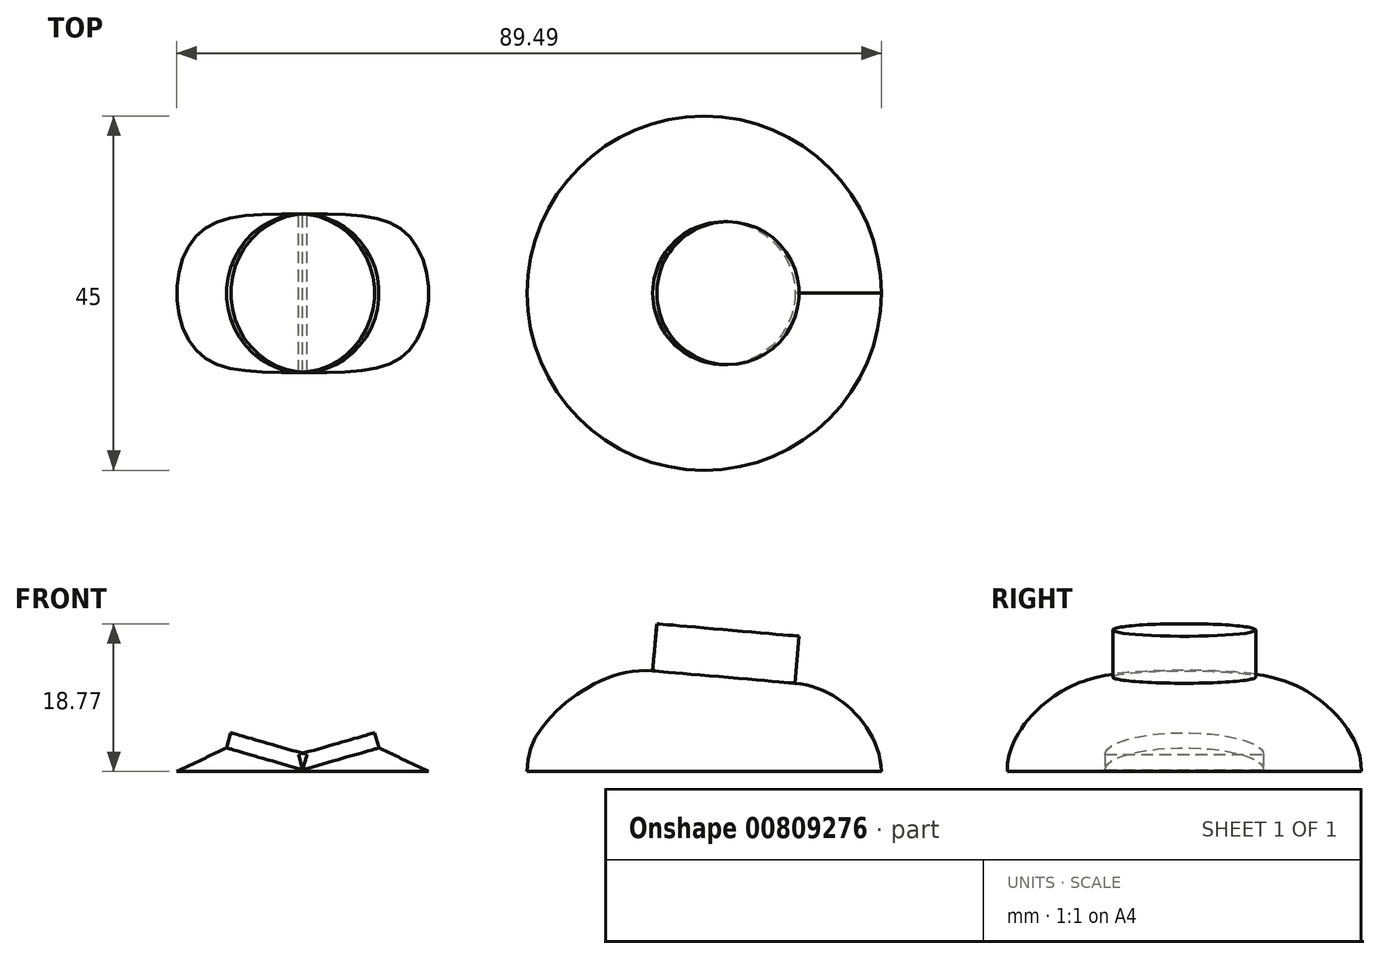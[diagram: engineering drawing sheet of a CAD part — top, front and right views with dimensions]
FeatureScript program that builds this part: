
annotation { "Feature Type Name" : "Feature", "Feature Type Description" : "" }
export const myFeature = defineFeature(function(context is Context, id is Id, definition is map)
    precondition{}
    {
        {
            var Q0;
            Q0=qCreatedBy(makeId("Top.planeOp"),FACE);
            cPlane(context, id + "F0", {"entities" : qUnion([Q0]), "cplaneType" : CPlaneType.OFFSET, "offset" : 12 * mm, "width" : 150 * mm, "height" : 150 * mm});
        }
        {
            var Q0;
            Q0=qCreatedBy(id+"F0.planeOp",FACE);
            var sketch = newSketch(context, id + "F1", { "sketchPlane" : qUnion([Q0])});
            skLineSegment(sketch, "E0", {"start": v(2.5, 4.56) * mm, "end": v(2.5, -4.56) * mm, "construction": true});
            skSolve(sketch);
        }
        {
            var Q0;
            Q0=sQuery(id+"F1.wireOp",EDGE,"E0");
            cPlane(context, id + "F2", {"entities" : qUnion([Q0]), "cplaneType" : CPlaneType.LINE_ANGLE, "offset" : 25 * mm, "angle" : 5 * degree, "oppositeDirection" : true, "width" : 150 * mm, "height" : 150 * mm});
        }
        {
            var Q0;
            Q0=qCreatedBy(id+"F2.planeOp",FACE);
            var sketch = newSketch(context, id + "F3", { "sketchPlane" : qUnion([Q0])});
            skPoint(sketch, "E1.0", {"position": v(1.44, 0) * mm});
            skCircle(sketch, "E2", {"center": v(1.44, 0) * mm, "radius": 9.07 * mm});
            skSolve(sketch);
        }
        {
            var Q0;
            Q0=qCreatedBy(makeId("Top.planeOp"),FACE);
            var sketch = newSketch(context, id + "F4", { "sketchPlane" : qUnion([Q0])});
            skCircle(sketch, "E3", {"center": v(0, 0) * mm, "radius": 22.5 * mm});
            skSolve(sketch);
        }
        {
            var Q0;
            Q0=qCreatedBy(makeId("Top.planeOp"),FACE);
            cPlane(context, id + "F5", {"entities" : qUnion([Q0]), "cplaneType" : CPlaneType.OFFSET, "offset" : 5 * mm, "width" : 150 * mm, "height" : 150 * mm});
        }
        {
            var Q0;
            Q0=qCreatedBy(id+"F5.planeOp",FACE);
            var sketch = newSketch(context, id + "F6", { "sketchPlane" : qUnion([Q0])});
            skCircle(sketch, "E4", {"center": v(0, 0) * mm, "radius": 21 * mm});
            skSolve(sketch);
        }
        {
            var Q0;
            Q0=makeQuery(id+"F4.imprint","IMPRINT",FACE,{"disambiguationData":[TD([[makeQuery(id+"F4.imprint","IMPRINT",EDGE,{"derivedFrom":sQuery(id+"F4.wireOp",EDGE,"E3")}),1.0]])]});
            var Q1;
            Q1=makeQuery(id+"F6.imprint","IMPRINT",FACE,{"disambiguationData":[TD([[makeQuery(id+"F6.imprint","IMPRINT",EDGE,{"derivedFrom":sQuery(id+"F6.wireOp",EDGE,"E4")}),1.0]])]});
            var Q2;
            Q2=makeQuery(id+"F3.imprint","IMPRINT",FACE,{"disambiguationData":[TD([[makeQuery(id+"F3.imprint","IMPRINT",EDGE,{"derivedFrom":sQuery(id+"F3.wireOp",EDGE,"E2")}),1.0]])]});
            loft(context, id + "F7", {"startCondition" : LoftEndDerivativeType.NORMAL_TO_PROFILE, "startMagnitude" : 1, "endCondition" : LoftEndDerivativeType.TANGENT_TO_PROFILE, "endMagnitude" : 1, "sheetProfilesArray" : [{ "sheetProfileEntities" : qUnion([Q0]) }, { "sheetProfileEntities" : qUnion([Q1]) }, { "sheetProfileEntities" : qUnion([Q2]) }]});
        }
        {
            var Q0;
            Q0=makeQuery(id+"F7.opLoft","CAP_FACE",FACE,{"disambiguationData":[OSD([makeQuery(id+"F3.imprint","IMPRINT",FACE,{"disambiguationData":[TD([[makeQuery(id+"F3.imprint","IMPRINT",EDGE,{"derivedFrom":sQuery(id+"F3.wireOp",EDGE,"E2")}),1.0]])]})])],"isStart":true});
            extrude(context, id + "F8", {"entities" : qUnion([Q0]), "operationType" : NewBodyOperationType.ADD, "depth" : 6 * mm, "offsetDistance" : 25 * mm});
        }
        {
            var Q0;
            Q0=qCreatedBy(makeId("Top.planeOp"),FACE);
            cPlane(context, id + "F9", {"entities" : qUnion([Q0]), "cplaneType" : CPlaneType.OFFSET, "offset" : 3 * mm, "width" : 150 * mm, "height" : 150 * mm});
        }
        {
            var Q0;
            Q0=qCreatedBy(id+"F9.planeOp",FACE);
            var sketch = newSketch(context, id + "F10", { "sketchPlane" : qUnion([Q0])});
            skLineSegment(sketch, "E5", {"start": v(-60.67, 23.33) * mm, "end": v(-60.67, -29.35) * mm, "construction": true});
            skSolve(sketch);
        }
        {
            var Q0;
            Q0=sQuery(id+"F10.wireOp",EDGE,"E5");
            cPlane(context, id + "F11", {"entities" : qUnion([Q0]), "cplaneType" : CPlaneType.LINE_ANGLE, "offset" : 25 * mm, "angle" : 16 * degree, "oppositeDirection" : true, "width" : 150 * mm, "height" : 150 * mm});
        }
        {
            var Q0;
            Q0=qCreatedBy(id+"F11.planeOp",FACE);
            var sketch = newSketch(context, id + "F12", { "sketchPlane" : qUnion([Q0])});
            skLineSegment(sketch, "E6.0", {"start": v(-59.15, -23.33) * mm, "end": v(-59.15, 29.35) * mm, "construction": true});
            skArc(sketch, "E7", {"start": v(-49.08, 10.07) * mm, "mid": v(-59.15, 0) * mm, "end": v(-49.08, -10.07) * mm});
            skLineSegment(sketch, "E8", {"start": v(-49.08, 10.07) * mm, "end": v(-49.08, -10.07) * mm});
            skSolve(sketch);
        }
        {
            var Q0;
            Q0=qCreatedBy(makeId("Top.planeOp"),FACE);
            var sketch = newSketch(context, id + "F13", { "sketchPlane" : qUnion([Q0])});
            skLineSegment(sketch, "E9.0", {"start": v(-50.99, -10.07) * mm, "end": v(-50.99, 10.07) * mm, "construction": true});
            skLineSegment(sketch, "E10", {"start": v(-66.99, -10.07) * mm, "end": v(-66.99, 10.07) * mm, "construction": true});
            skFitSpline(sketch, "E11", {"points": [v(-50.99, -10.07) * mm, v(-63.74, -8) * mm, v(-66.99, 0) * mm, v(-63.74, 7.95) * mm, v(-50.99, 10.07) * mm], "startDerivative": vector(-65.21, 0) * mm, "endDerivative": vector(65.3, 0) * mm});
            skLineSegment(sketch, "E12", {"start": v(-50.99, -10.07) * mm, "end": v(-66.99, -10.07) * mm, "construction": true});
            skLineSegment(sketch, "E13", {"start": v(-66.99, 10.07) * mm, "end": v(-50.99, 10.07) * mm, "construction": true});
            skLineSegment(sketch, "E14", {"start": v(-63.74, -10.07) * mm, "end": v(-63.74, 10.07) * mm, "construction": true});
            skLineSegment(sketch, "E15", {"start": v(-50.99, -10.07) * mm, "end": v(-50.99, 10.07) * mm});
            skSolve(sketch);
        }
        {
            var Q0;
            Q0=makeQuery(id+"F13.imprint","IMPRINT",FACE,{"disambiguationData":[TD([[makeQuery(id+"F13.imprint","IMPRINT",EDGE,{"derivedFrom":sQuery(id+"F13.wireOp",EDGE,"E11")}),-1.0]])]});
            var Q1;
            Q1=makeQuery(id+"F12.imprint","IMPRINT",FACE,{"disambiguationData":[TD([[makeQuery(id+"F12.imprint","IMPRINT",EDGE,{"derivedFrom":sQuery(id+"F12.wireOp",EDGE,"E7")}),1.0]])]});
            loft(context, id + "F14", {"sheetProfilesArray" : [{ "sheetProfileEntities" : qUnion([Q0]) }, { "sheetProfileEntities" : qUnion([Q1]) }]});
        }
        {
            var Q0;
            Q0=makeQuery(id+"F12.imprint","IMPRINT",FACE,{"disambiguationData":[TD([[makeQuery(id+"F12.imprint","IMPRINT",EDGE,{"derivedFrom":sQuery(id+"F12.wireOp",EDGE,"E7")}),1.0]])]});
            extrude(context, id + "F15", {"entities" : qUnion([Q0]), "operationType" : NewBodyOperationType.ADD, "oppositeDirection" : true, "depth" : 2 * mm, "offsetDistance" : 25 * mm});
        }
        {
            var Q0;
            Q0=makeQuery(id+"F14.opLoft","SWEPT_BODY",BODY,{"disambiguationData":[OSD([makeQuery(id+"F12.imprint","IMPRINT",FACE,{"disambiguationData":[TD([[makeQuery(id+"F12.imprint","IMPRINT",EDGE,{"derivedFrom":sQuery(id+"F12.wireOp",EDGE,"E7")}),1.0]])]}),makeQuery(id+"F13.imprint","IMPRINT",FACE,{"disambiguationData":[TD([[makeQuery(id+"F13.imprint","IMPRINT",EDGE,{"derivedFrom":sQuery(id+"F13.wireOp",EDGE,"E11")}),-1.0]])]})])]});
            var Q1;
            {var subQ0=sQuery(id+"F13.wireOp",EDGE,"E15");var subQ1=sQuery(id+"F13.wireOp",EDGE,"E11");var subQ2=sQuery(id+"F12.wireOp",EDGE,"E8");var subQ3=sQuery(id+"F12.wireOp",EDGE,"E7");Q1=makeQuery(id+"F14.opLoft","SWEPT_FACE",FACE,{"disambiguationData":[OSD([subQ3,subQ2,subQ1,subQ0]),TDD([makeQuery(id+"F12.imprint","INTERSECT",VERTEX,{"disambiguationData":[OD(0.0)],"derivedFrom":[subQ3,subQ2]}),makeQuery(id+"F12.imprint","INTERSECT",VERTEX,{"disambiguationData":[OD(1.0)],"derivedFrom":[subQ3,subQ2]}),makeQuery(id+"F12.imprint","IMPRINT",EDGE,{"derivedFrom":subQ2}),makeQuery(id+"F13.imprint","INTERSECT",VERTEX,{"disambiguationData":[OD(0.0)],"derivedFrom":[subQ1,subQ0]}),makeQuery(id+"F13.imprint","INTERSECT",VERTEX,{"disambiguationData":[OD(1.0)],"derivedFrom":[subQ1,subQ0]}),makeQuery(id+"F13.imprint","IMPRINT",EDGE,{"derivedFrom":subQ0})])]});}
            mirror(context, id + "F16", {"operationType" : NewBodyOperationType.ADD, "entities" : qUnion([Q0]), "mirrorPlane" : qUnion([Q1])});
        }
    });
